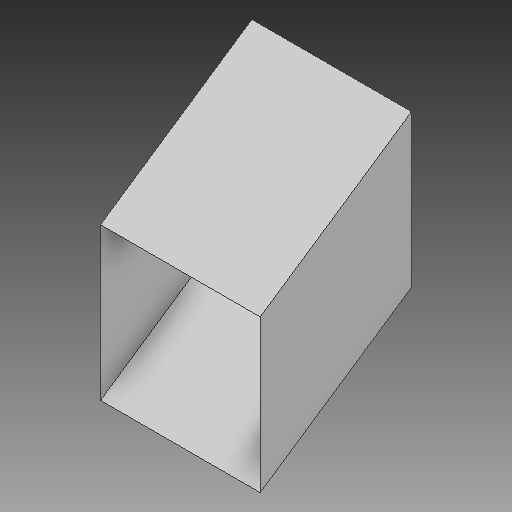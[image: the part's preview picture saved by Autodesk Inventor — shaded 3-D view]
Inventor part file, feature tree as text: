
AUTODESK INVENTOR PART (.ipt)
format: ipt  version: 2017 (Build 210142000, 142)  size: 91,648 bytes
history: native  units: in
note: dims shown in document units (in); Inventor stores cm internally (conversion verified against a paired STEP export)
features: other x2, sketch x2
ambient origin geometry x8: Origin, YZ Plane, XZ Plane, XY Plane, X Axis, Y Axis, Z Axis, Center Point
bodies: Solid1 (feature_tree)
feature tree (4):
  other  "ramp"
  other  "removed ends"
  sketch  "Sketch1"  dims[d0=7.0in]
  sketch  "Sketch2"  dims[d1=6.6667in d2=0.8521in d3=8.0in d4=0.0in d5=0.0in]
